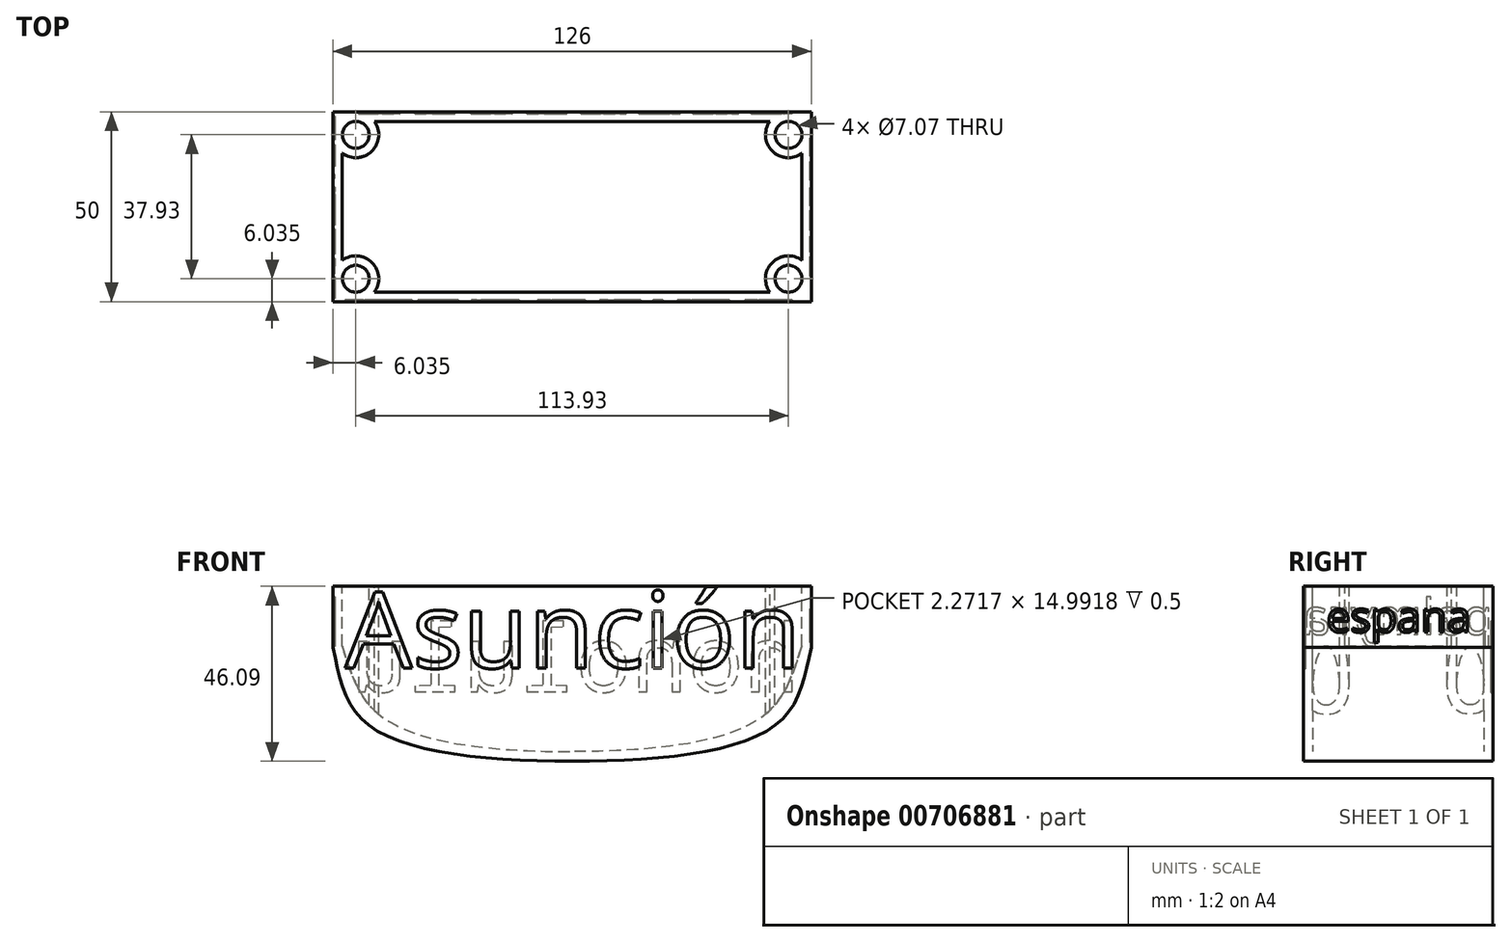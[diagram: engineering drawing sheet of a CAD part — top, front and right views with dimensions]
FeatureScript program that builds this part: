
annotation { "Feature Type Name" : "Feature", "Feature Type Description" : "" }
export const myFeature = defineFeature(function(context is Context, id is Id, definition is map)
    precondition{}
    {
        {
            var Q0;
            Q0=qCreatedBy(makeId("Front.planeOp"),FACE);
            var sketch = newSketch(context, id + "F0", { "sketchPlane" : qUnion([Q0])});
            skFitSpline(sketch, "E0", {"points": [v(-63, 0) * mm, v(-51.25, -20.56) * mm, v(0, -30) * mm, v(53.49, -20.56) * mm, v(63, 0) * mm], "startDerivative": vector(36.9, -122.21) * mm, "endDerivative": vector(28.83, 130.56) * mm});
            skLineSegment(sketch, "E1.bottom", {"start": v(-63, 0) * mm, "end": v(63, 0) * mm});
            skLineSegment(sketch, "E1.top", {"start": v(-63, 16.1) * mm, "end": v(63, 16.1) * mm});
            skLineSegment(sketch, "E1.left", {"start": v(-63, 0) * mm, "end": v(-63, 16.1) * mm});
            skLineSegment(sketch, "E1.right", {"start": v(63, 0) * mm, "end": v(63, 16.1) * mm});
            skSolve(sketch);
        }
        {
            var Q0;
            Q0 = qSketchRegion(id + "F0", true);
            extrude(context, id + "F1", {"entities" : qUnion([Q0]), "endBound" : BoundingType.SYMMETRIC, "depth" : 50 * mm, "offsetDistance" : 25 * mm});
        }
        {
            var Q0;
            Q0=makeQuery(id+"F1.opExtrude","SWEPT_FACE",FACE,{"disambiguationData":[OSD([sQuery(id+"F0.wireOp",EDGE,"E1.top")])]});
            shell(context, id + "F2", {"entities" : qUnion([Q0]), "thickness" : 2.5 * mm});
        }
        {
            var Q0;
            Q0=makeQuery(id+"F1.opExtrude","SWEPT_FACE",FACE,{"disambiguationData":[OSD([sQuery(id+"F0.wireOp",EDGE,"E1.top")])]});
            var sketch = newSketch(context, id + "F3", { "sketchPlane" : qUnion([Q0])});
            skCircle(sketch, "E2", {"center": v(-56.96, -18.96) * mm, "radius": 6.04 * mm});
            skCircle(sketch, "E3", {"center": v(-56.96, -18.96) * mm, "radius": 3.54 * mm});
            skSolve(sketch);
        }
        {
            var Q0;
            Q0 = qSketchRegion(id + "F3", true);
            var Q1;
            Q1=makeQuery(id+"F1.opExtrude","SWEPT_FACE",FACE,{"disambiguationData":[OSD([sQuery(id+"F0.wireOp",EDGE,"E0")])]});
            extrude(context, id + "F4", {"entities" : qUnion([Q0]), "operationType" : NewBodyOperationType.ADD, "endBound" : BoundingType.UP_TO_SURFACE, "oppositeDirection" : true, "depth" : 25 * mm, "endBoundEntityFace" : qUnion([Q1]), "offsetDistance" : 25 * mm});
        }
        {
            var Q0;
            Q0=makeQuery(id+"F1.opExtrude","SWEPT_BODY",BODY,{"disambiguationData":[OSD([sQuery(id+"F0.wireOp",EDGE,"E0"),sQuery(id+"F0.wireOp",EDGE,"E1.top"),sQuery(id+"F0.wireOp",EDGE,"E1.left"),sQuery(id+"F0.wireOp",EDGE,"E1.right")])]});
            var Q1;
            Q1=qCreatedBy(makeId("Front.planeOp"),FACE);
            mirror(context, id + "F5", {"operationType" : NewBodyOperationType.ADD, "entities" : qUnion([Q0]), "mirrorPlane" : qUnion([Q1])});
        }
        {
            var Q0;
            Q0=makeQuery(id+"F1.opExtrude","SWEPT_BODY",BODY,{"disambiguationData":[OSD([sQuery(id+"F0.wireOp",EDGE,"E0"),sQuery(id+"F0.wireOp",EDGE,"E1.top"),sQuery(id+"F0.wireOp",EDGE,"E1.left"),sQuery(id+"F0.wireOp",EDGE,"E1.right")])]});
            var Q1;
            Q1=qCreatedBy(makeId("Right.planeOp"),FACE);
            mirror(context, id + "F6", {"operationType" : NewBodyOperationType.ADD, "entities" : qUnion([Q0]), "mirrorPlane" : qUnion([Q1])});
        }
        {
            var Q0;
            Q0=makeQuery(id+"F1.opExtrude","SWEPT_FACE",FACE,{"disambiguationData":[OSD([sQuery(id+"F0.wireOp",EDGE,"E1.right")])]});
            var sketch = newSketch(context, id + "F7", { "sketchPlane" : qUnion([Q0])});
            skText(sketch, "E4", { "text": "espana", "fontName": "OpenSans-Regular.ttf"});
            const initialGuessF7  = {"E4": [-0.01889, 0.004, 1, 0, 0.0081]};
            skSetInitialGuess(sketch, initialGuessF7);
            skSolve(sketch);
        }
        {
            var Q0;
            Q0 = qSketchRegion(id + "F7", true);
            extrude(context, id + "F8", {"entities" : qUnion([Q0]), "operationType" : NewBodyOperationType.REMOVE, "oppositeDirection" : true, "depth" : 0.3 * mm, "offsetDistance" : 25 * mm});
        }
        {
            var Q0;
            {var subQ0=makeQuery(id+"F1.opExtrude","CAP_FACE",FACE,{"disambiguationData":[OSD([sQuery(id+"F0.wireOp",EDGE,"E0"),sQuery(id+"F0.wireOp",EDGE,"E1.top"),sQuery(id+"F0.wireOp",EDGE,"E1.left"),sQuery(id+"F0.wireOp",EDGE,"E1.right")])],"isStart":true});Q0=makeQuery(id+"F6.boolean.opBoolean","MERGE",FACE,{"derivedFrom":[subQ0,makeQuery(id+"F6.opPattern","COPY",FACE,{"derivedFrom":subQ0,"instanceName":"1"})]});}
            var sketch = newSketch(context, id + "F9", { "sketchPlane" : qUnion([Q0])});
            skText(sketch, "E5", { "text": "honolulu", "fontName": "DroidSansMono.ttf"});
            const initialGuessF9  = {"E5": [-0.05992, -0.0117, 1, 0, 0.0177]};
            skSetInitialGuess(sketch, initialGuessF9);
            skSolve(sketch);
        }
        {
            var Q0;
            Q0 = qSketchRegion(id + "F9", true);
            extrude(context, id + "F10", {"entities" : qUnion([Q0]), "operationType" : NewBodyOperationType.REMOVE, "oppositeDirection" : true, "depth" : 0.5 * mm, "offsetDistance" : 25 * mm});
        }
        {
            var Q0;
            Q0=makeQuery(id+"F1.opExtrude","SWEPT_FACE",FACE,{"disambiguationData":[OSD([sQuery(id+"F0.wireOp",EDGE,"E1.left")])]});
            var sketch = newSketch(context, id + "F11", { "sketchPlane" : qUnion([Q0])});
            skText(sketch, "E6", { "text": "palmyra", "fontName": "OpenSans-Regular.ttf"});
            const initialGuessF11  = {"E6": [-0.025, 0.00338, 1, 0, 0.00946]};
            skSetInitialGuess(sketch, initialGuessF11);
            skSolve(sketch);
        }
        {
            var Q0;
            Q0 = qSketchRegion(id + "F11", true);
            extrude(context, id + "F12", {"entities" : qUnion([Q0]), "operationType" : NewBodyOperationType.REMOVE, "oppositeDirection" : true, "depth" : 0.5 * mm, "offsetDistance" : 25 * mm});
        }
        {
            var Q0;
            {var subQ0=makeQuery(id+"F1.opExtrude","CAP_FACE",FACE,{"disambiguationData":[OSD([sQuery(id+"F0.wireOp",EDGE,"E0"),sQuery(id+"F0.wireOp",EDGE,"E1.top"),sQuery(id+"F0.wireOp",EDGE,"E1.left"),sQuery(id+"F0.wireOp",EDGE,"E1.right")])],"isStart":false});Q0=makeQuery(id+"F6.boolean.opBoolean","MERGE",FACE,{"derivedFrom":[subQ0,makeQuery(id+"F6.opPattern","COPY",FACE,{"derivedFrom":subQ0,"instanceName":"1"})]});}
            var sketch = newSketch(context, id + "F13", { "sketchPlane" : qUnion([Q0])});
            skText(sketch, "E7", { "text": "Asunción", "fontName": "OpenSans-Regular.ttf"});
            const initialGuessF13  = {"E7": [-0.0598, -0.00544, 1, 0, 0.02017]};
            skSetInitialGuess(sketch, initialGuessF13);
            skSolve(sketch);
        }
        {
            var Q0;
            Q0 = qSketchRegion(id + "F13", true);
            extrude(context, id + "F14", {"entities" : qUnion([Q0]), "operationType" : NewBodyOperationType.REMOVE, "oppositeDirection" : true, "depth" : 0.5 * mm, "offsetDistance" : 25 * mm});
        }
    });
